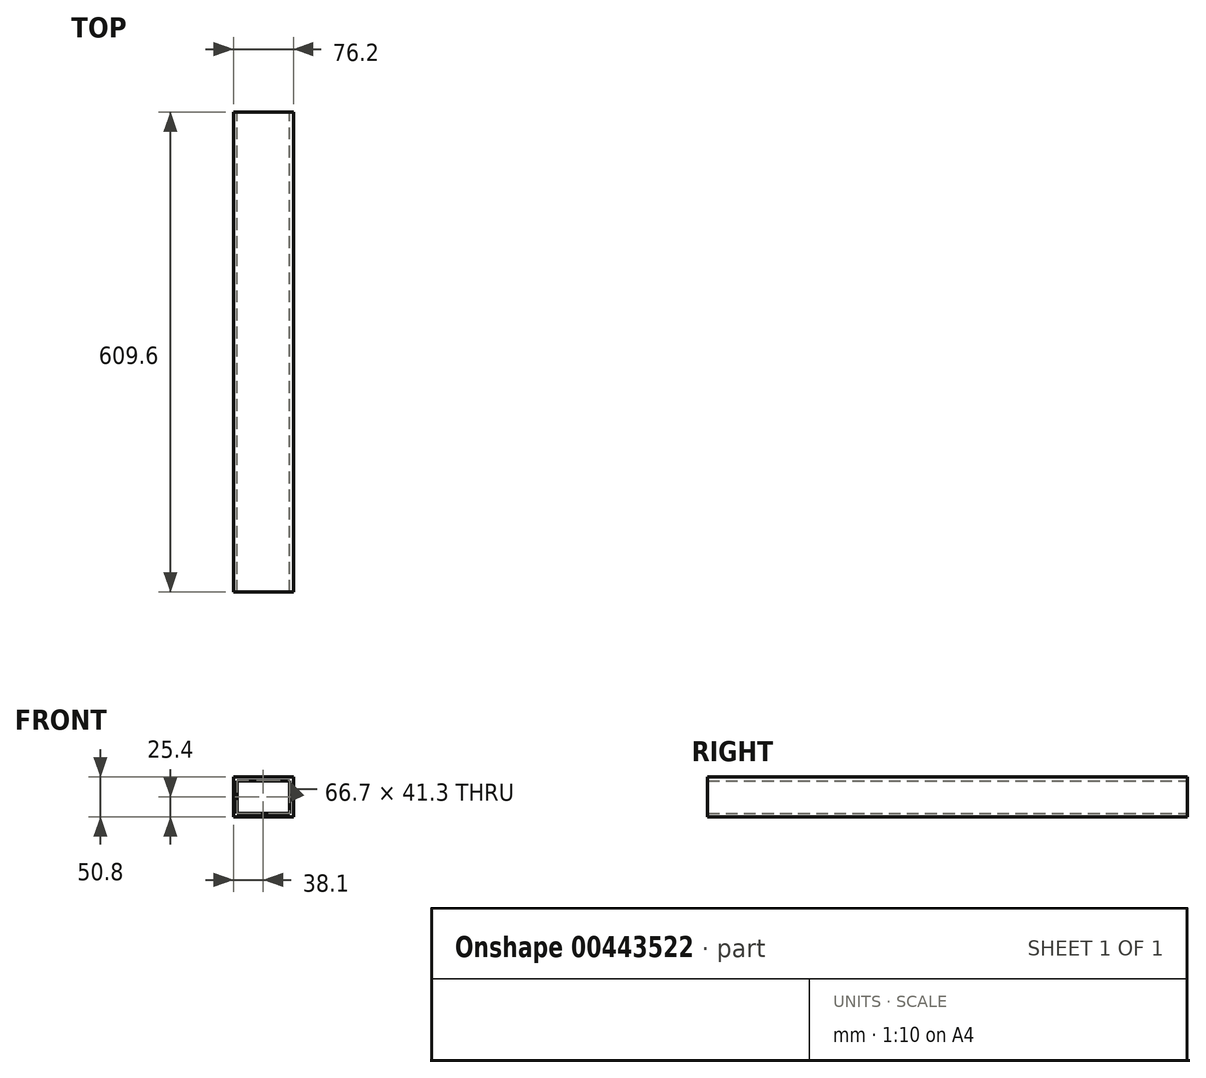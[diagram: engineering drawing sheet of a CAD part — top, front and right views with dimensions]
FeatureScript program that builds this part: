
annotation { "Feature Type Name" : "Feature", "Feature Type Description" : "" }
export const myFeature = defineFeature(function(context is Context, id is Id, definition is map)
    precondition{}
    {
        {
            var Q0;
            Q0=qCreatedBy(makeId("Front.planeOp"),FACE);
            var sketch = newSketch(context, id + "F0", { "sketchPlane" : qUnion([Q0])});
            skLineSegment(sketch, "E0.bottom", {"start": v(-38.1, 25.4) * mm, "end": v(38.1, 25.4) * mm});
            skLineSegment(sketch, "E0.top", {"start": v(-38.1, -25.4) * mm, "end": v(38.1, -25.4) * mm});
            skLineSegment(sketch, "E0.left", {"start": v(-38.1, 25.4) * mm, "end": v(-38.1, -25.4) * mm});
            skLineSegment(sketch, "E0.right", {"start": v(38.1, 25.4) * mm, "end": v(38.1, -25.4) * mm});
            skLineSegment(sketch, "E1.bottom", {"start": v(-33.35, 20.65) * mm, "end": v(33.35, 20.65) * mm});
            skLineSegment(sketch, "E1.top", {"start": v(-33.35, -20.65) * mm, "end": v(33.35, -20.65) * mm});
            skLineSegment(sketch, "E1.left", {"start": v(-33.35, 20.65) * mm, "end": v(-33.35, -20.65) * mm});
            skLineSegment(sketch, "E1.right", {"start": v(33.35, 20.65) * mm, "end": v(33.35, -20.65) * mm});
            skSolve(sketch);
        }
        {
            var Q0;
            Q0=makeQuery(id+"F0.imprint","IMPRINT",FACE,{"disambiguationData":[TD([[makeQuery(id+"F0.imprint","IMPRINT",EDGE,{"derivedFrom":sQuery(id+"F0.wireOp",EDGE,"E0.bottom")}),-1.0]])]});
            extrude(context, id + "F1", {"entities" : qUnion([Q0]), "depth" : 609.6 * mm});
        }
    });
